# Revit family: bimlib_narujnyeblokisistemakondicionirovaniya_mrv-5-rc_16-22hp_haier
name_source: partatom
category: Оборудование
units: mm (PartAtom-declared; Revit-internal decimal feet)

## family parameters
Всегда вертикально = Да
На основе рабочей плоскости = Нет
Общий = Нет
При загрузке вырезать с полостями = Нет
Размер круглого соединителя = Использовать диаметр
Тип детали = Нормальный
Точка расчета площади = Нет

## types (4) — shared parameters
ADSK_URL документации изделия = https://haierproff.ru
ADSK_URL страницы изделия = https://haierproff.ru
ADSK_Версия Revit = 2017
ADSK_Группирование = VRF-системы MRV 5-RC
ADSK_Единица измерения = шт.
ADSK_Завод-изготовитель = Haier Group
ADSK_Классификация нагрузок = ОВК
ADSK_Количество = 1
ADSK_Количество фаз = 3
ADSK_Коэффициент мощности = 1
ADSK_Напряжение = 400 В
ADSK_Обозначение = MRV 5-RC
ADSK_Размер_Высота = 1690 мм
ADSK_Размер_Глубина = 750 мм
ADSK_Размер_Ширина = 1410 мм
BL_BIM library = https://bimlib.pro
HG_URL поставщика = www.haierproff.ru
URL = www.haier.com
Диаметр_Газ = 28.58 мм
Диаметр_Газовой линии нагнетания = 25.4 мм
Заправка хладагента = 10.00 кг
Изготовитель = Haier Group
Производитель компрессора = MITSUBISHI ELECTRIC
Работа на обогрев = Нет
Рабочий диапазон_Обогрев = -23 ~ 21
Рабочий диапазон_Охлаждение = -5 ~ 50
Тип компрессора = DC INV. СПИРАЛ.
Тип хладагента = R410A
Частота тока = 50 Гц
zero-valued in all types: Отметка по умолчанию

## per-type parameters (varying)
| type | ADSK_Код изделия | ADSK_Масса | ADSK_Наименование | ADSK_Наименование краткое | ADSK_Номинальная мощность | ADSK_Полная мощность | ADSK_Расход воздуха | Диаметр_Жидкость | Звуковая мощность | Звуковое давление | Обогрев_Максимальная потребляемая мощность | Обогрев_Максимальный ток | Обогрев_Номинальная потребляемая мощность | Обогрев_Номинальный ток | Охлаждение_Максимальная потребляемая мощность | Охлаждение_Максимальный ток | Охлаждение_Номинальная потребляемая мощность | Охлаждение_Номинальный ток | Теплопроизводительность | Холодопроизводительность |
| AV18IMVURA_18HP_HAIER | AV18IMVURA | 366 | Наружный блок VRF-системы кондиционирования MRV 5-RC, 18HP | VRF-системы MRV 5-RC, 18HP | 14750 Вт | 14750 В·А | 17000.0 м³/ч | 15.88 мм | 84 | 63 | 26 кВт | 42 А | 14 кВт | 24 А | 29 кВт | 47 А | 15 кВт | 24 А | 56 кВт | 50 кВт |
| AV20IMVURA_20HP_HAIER | AV20IMVURA | 375 | Наружный блок VRF-системы кондиционирования MRV 5-RC, 20HP | VRF-системы MRV 5-RC, 20HP | 16920 Вт | 16920 В·А | 19000.0 м³/ч | 15.88 мм | 84 | 63 | 29 кВт | 49 А | 16 кВт | 27 А | 32 кВт | 53 А | 17 кВт | 28 А | 63 кВт | 56 кВт |
| AV22IMVURA_22HP_HAIER | AV22IMVURA | 375 | Наружный блок VRF-системы кондиционирования MRV 5-RC, 22HP | VRF-системы MRV 5-RC, 22HP | 19570 Вт | 19570 В·А | 19000.0 м³/ч | 15.88 мм | 85 | 64 | 30 кВт | 50 А | 19 кВт | 31 А | 33 кВт | 55 А | 20 кВт | 32 А | 69 кВт | 63 кВт |
| AV16IMVURA_16HP_HAIER | AV16IMVURA | 366 | Наружный блок VRF-системы кондиционирования MRV 5-RC, 16HP | VRF-системы MRV 5-RC, 16HP | 12680 Вт | 12680 В·А | 17000.0 м³/ч | 12.7 мм | 83 | 62 | 23 кВт | 37 А | 12 кВт | 20 А | 25 кВт | 41 А | 13 кВт | 21 А | 60 кВт | 45 кВт |
